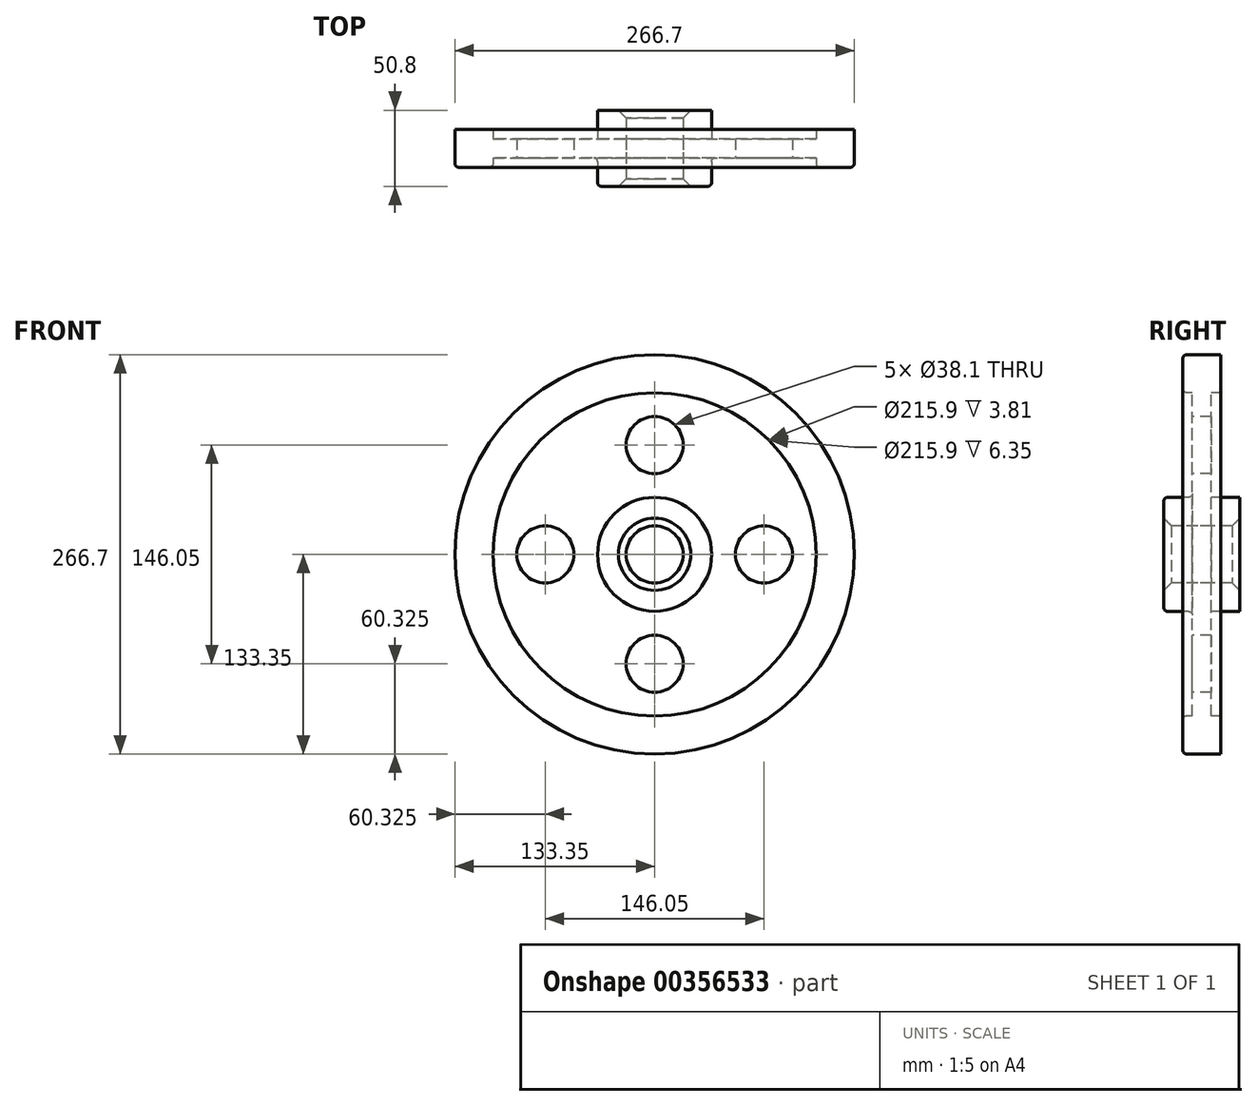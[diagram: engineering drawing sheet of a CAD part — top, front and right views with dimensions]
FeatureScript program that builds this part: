
annotation { "Feature Type Name" : "Feature", "Feature Type Description" : "" }
export const myFeature = defineFeature(function(context is Context, id is Id, definition is map)
    precondition{}
    {
        {
            var Q0;
            Q0=qCreatedBy(makeId("Right.planeOp"),FACE);
            var sketch = newSketch(context, id + "F0", { "sketchPlane" : qUnion([Q0])});
            skLineSegment(sketch, "E0", {"start": v(0, 0) * mm, "end": v(25.4, 0) * mm});
            skLineSegment(sketch, "E1.0", {"start": v(0, 19.05) * mm, "end": v(25.4, 19.05) * mm});
            skLineSegment(sketch, "E2.0", {"start": v(6.35, 38.1) * mm, "end": v(25.4, 38.1) * mm});
            skLineSegment(sketch, "E3.0", {"start": v(6.35, 107.95) * mm, "end": v(12.7, 107.95) * mm});
            skLineSegment(sketch, "E4.0", {"start": v(0, 133.35) * mm, "end": v(12.7, 133.35) * mm});
            skLineSegment(sketch, "E5.0", {"start": v(12.7, 133.35) * mm, "end": v(12.7, 107.95) * mm});
            skLineSegment(sketch, "E6.0", {"start": v(6.35, 107.95) * mm, "end": v(6.35, 38.1) * mm});
            skLineSegment(sketch, "E7.0", {"start": v(25.4, 38.1) * mm, "end": v(25.4, 19.05) * mm});
            skLineSegment(sketch, "E8", {"start": v(0, 133.35) * mm, "end": v(0, 19.05) * mm});
            skLineSegment(sketch, "E9.MirrorCS", {"start": v(0, 133.35) * mm, "end": v(-12.7, 133.35) * mm});
            skLineSegment(sketch, "E10.MirrorCS", {"start": v(-12.7, 133.35) * mm, "end": v(-12.7, 107.95) * mm});
            skLineSegment(sketch, "E11.MirrorCS", {"start": v(-6.35, 107.95) * mm, "end": v(-6.35, 38.1) * mm});
            skLineSegment(sketch, "E12.MirrorCS", {"start": v(-25.4, 38.1) * mm, "end": v(-25.4, 19.05) * mm});
            skLineSegment(sketch, "E13.MirrorCS", {"start": v(0, 19.05) * mm, "end": v(-25.4, 19.05) * mm});
            skLineSegment(sketch, "E14.MirrorCS", {"start": v(-6.35, 38.1) * mm, "end": v(-25.4, 38.1) * mm});
            skLineSegment(sketch, "E15.MirrorCS", {"start": v(-6.35, 107.95) * mm, "end": v(-12.7, 107.95) * mm});
            skSolve(sketch);
        }
        {
            var Q0;
            Q0=makeQuery(id+"F0.imprint","IMPRINT",FACE,{"disambiguationData":[TD([[makeQuery(id+"F0.imprint","IMPRINT",EDGE,{"derivedFrom":sQuery(id+"F0.wireOp",EDGE,"E1.0")}),1.0]])]});
            var Q1;
            Q1=makeQuery(id+"F0.imprint","IMPRINT",FACE,{"disambiguationData":[TD([[makeQuery(id+"F0.imprint","IMPRINT",EDGE,{"derivedFrom":sQuery(id+"F0.wireOp",EDGE,"E8")}),-1.0]])]});
            var Q2;
            Q2=sQuery(id+"F0.wireOp",EDGE,"E0");
            revolve(context, id + "F1", {"entities" : qUnion([Q0, Q1]), "axis" : qUnion([Q2]), "revolveType" : RevolveType.FULL});
        }
        {
            var Q0;
            Q0=makeQuery(id+"F1.opRevolve","SWEPT_FACE",FACE,{"disambiguationData":[OSD([sQuery(id+"F0.wireOp",EDGE,"E11.MirrorCS")])]});
            var sketch = newSketch(context, id + "F2", { "sketchPlane" : qUnion([Q0])});
            skLineSegment(sketch, "E16", {"start": v(0, 0) * mm, "end": v(0, 73.03) * mm});
            skCircle(sketch, "E17", {"center": v(0, 73.03) * mm, "radius": 19.05 * mm});
            skCircle(sketch, "E18.1.0", {"center": v(-73.03, 0) * mm, "radius": 19.05 * mm});
            skCircle(sketch, "E18.2.0", {"center": v(0, -73.03) * mm, "radius": 19.05 * mm});
            skCircle(sketch, "E18.3.0", {"center": v(73.03, 0) * mm, "radius": 19.05 * mm});
            skPoint(sketch, "E18.center", {"position": v(0, 0) * mm});
            skSolve(sketch);
        }
        {
            var Q0;
            Q0=makeQuery(id+"F2.imprint","IMPRINT",FACE,{"disambiguationData":[TD([[makeQuery(id+"F2.imprint","IMPRINT",EDGE,{"derivedFrom":sQuery(id+"F2.wireOp",EDGE,"E17")}),1.0]])]});
            var Q1;
            Q1=makeQuery(id+"F2.imprint","IMPRINT",FACE,{"disambiguationData":[TD([[makeQuery(id+"F2.imprint","IMPRINT",EDGE,{"derivedFrom":sQuery(id+"F2.wireOp",EDGE,"E18.3.0")}),1.0]])]});
            var Q2;
            Q2=makeQuery(id+"F2.imprint","IMPRINT",FACE,{"disambiguationData":[TD([[makeQuery(id+"F2.imprint","IMPRINT",EDGE,{"derivedFrom":sQuery(id+"F2.wireOp",EDGE,"E18.2.0")}),1.0]])]});
            var Q3;
            Q3=makeQuery(id+"F2.imprint","IMPRINT",FACE,{"disambiguationData":[TD([[makeQuery(id+"F2.imprint","IMPRINT",EDGE,{"derivedFrom":sQuery(id+"F2.wireOp",EDGE,"E18.1.0")}),1.0]])]});
            extrude(context, id + "F3", {"entities" : qUnion([Q0, Q1, Q2, Q3]), "operationType" : NewBodyOperationType.REMOVE, "oppositeDirection" : true, "depth" : 25.4 * mm});
        }
        {
            var Q0;
            Q0=makeQuery(id+"F1.opRevolve","SWEPT_EDGE",EDGE,{"disambiguationData":[OSD([sQuery(id+"F0.wireOp",EDGE,"E12.MirrorCS"),sQuery(id+"F0.wireOp",EDGE,"E14.MirrorCS")])]});
            var Q1;
            Q1=makeQuery(id+"F1.opRevolve","SWEPT_EDGE",EDGE,{"disambiguationData":[OSD([sQuery(id+"F0.wireOp",EDGE,"E11.MirrorCS"),sQuery(id+"F0.wireOp",EDGE,"E14.MirrorCS")])]});
            var Q2;
            Q2=makeQuery(id+"F1.opRevolve","SWEPT_EDGE",EDGE,{"disambiguationData":[OSD([sQuery(id+"F0.wireOp",EDGE,"E10.MirrorCS"),sQuery(id+"F0.wireOp",EDGE,"E15.MirrorCS")])]});
            var Q3;
            Q3=makeQuery(id+"F1.opRevolve","SWEPT_EDGE",EDGE,{"disambiguationData":[OSD([sQuery(id+"F0.wireOp",EDGE,"E9.MirrorCS"),sQuery(id+"F0.wireOp",EDGE,"E10.MirrorCS")])]});
            fillet(context, id + "F4", {"entities" : qUnion([Q0, Q1, Q2, Q3]), "radius" : 2.54 * mm, "tangentPropagation" : true, "allowEdgeOverflow" : false});
        }
        {
            var Q0;
            Q0=makeQuery(id+"F1.opRevolve","SWEPT_EDGE",EDGE,{"disambiguationData":[OSD([sQuery(id+"F0.wireOp",EDGE,"E12.MirrorCS"),sQuery(id+"F0.wireOp",EDGE,"E13.MirrorCS")])]});
            var Q1;
            Q1=makeQuery(id+"F1.opRevolve","SWEPT_EDGE",EDGE,{"disambiguationData":[OSD([sQuery(id+"F0.wireOp",EDGE,"E1.0"),sQuery(id+"F0.wireOp",EDGE,"E7.0")])]});
            chamfer(context, id + "F5", {"entities" : qUnion([Q0, Q1]), "width" : 5.08 * mm, "tangentPropagation" : true});
        }
    });
